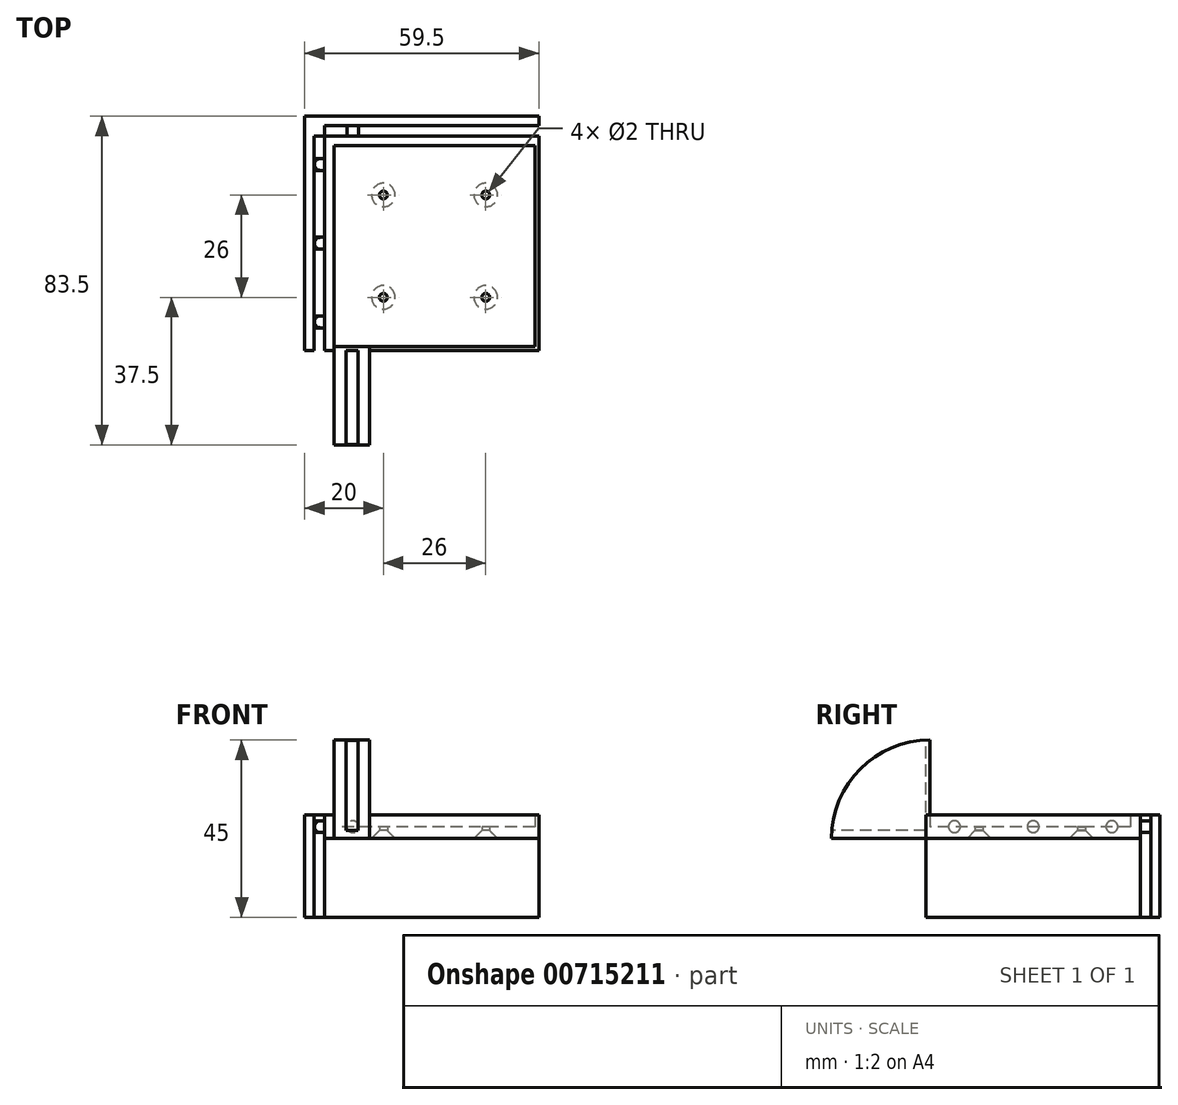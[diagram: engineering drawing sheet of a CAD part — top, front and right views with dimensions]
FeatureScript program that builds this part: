
annotation { "Feature Type Name" : "Feature", "Feature Type Description" : "" }
export const myFeature = defineFeature(function(context is Context, id is Id, definition is map)
    precondition{}
    {
        {
            var Q0;
            Q0=qCreatedBy(makeId("Top.planeOp"),FACE);
            var sketch = newSketch(context, id + "F0", { "sketchPlane" : qUnion([Q0])});
            skLineSegment(sketch, "E0.bottom", {"start": v(25.5, 25.5) * mm, "end": v(-25.5, 25.5) * mm});
            skLineSegment(sketch, "E0.top", {"start": v(25.5, -25.5) * mm, "end": v(-22.25, -25.5) * mm});
            skLineSegment(sketch, "E0.left", {"start": v(25.5, 25.5) * mm, "end": v(25.5, -25.5) * mm});
            skLineSegment(sketch, "E0.right", {"start": v(-25.5, 25.5) * mm, "end": v(-25.5, -25.5) * mm});
            skPoint(sketch, "E0.middle", {"position": v(0, 0) * mm});
            skLineSegment(sketch, "E1.0", {"start": v(28, 28) * mm, "end": v(-28, 28) * mm});
            skLineSegment(sketch, "E1.1", {"start": v(28, 28) * mm, "end": v(28, -28) * mm});
            skLineSegment(sketch, "E1.2", {"start": v(28, -28) * mm, "end": v(-22.25, -28) * mm});
            skLineSegment(sketch, "E1.3", {"start": v(-28, 28) * mm, "end": v(-28, -28) * mm});
            skCircle(sketch, "E2", {"center": v(-13, 13) * mm, "radius": 1 * mm});
            skLineSegment(sketch, "E3", {"start": v(0, 28) * mm, "end": v(0, -28) * mm, "construction": true});
            skLineSegment(sketch, "E4", {"start": v(-28, 0) * mm, "end": v(28, 0) * mm, "construction": true});
            skCircle(sketch, "E5.MirrorC", {"center": v(13, 13) * mm, "radius": 1 * mm});
            skCircle(sketch, "E6.MirrorC", {"center": v(13, -13) * mm, "radius": 1 * mm});
            skCircle(sketch, "E7.MirrorC", {"center": v(-13, -13) * mm, "radius": 1 * mm});
            skLineSegment(sketch, "E8.1", {"start": v(28, 33) * mm, "end": v(-33, 33) * mm});
            skLineSegment(sketch, "E9", {"start": v(28, 33) * mm, "end": v(28, 28) * mm});
            skLineSegment(sketch, "E10", {"start": v(-28, -28) * mm, "end": v(-33, -28) * mm});
            skLineSegment(sketch, "E11", {"start": v(28, 23.2) * mm, "end": v(28, 12.96) * mm});
            skLineSegment(sketch, "E12", {"start": v(28, 23.2) * mm, "end": v(28, 20) * mm});
            skLineSegment(sketch, "E13.trimOffspring", {"start": v(-25.25, -28) * mm, "end": v(-28, -28) * mm});
            skLineSegment(sketch, "E14", {"start": v(-25.5, -25.5) * mm, "end": v(-22.25, -25.5) * mm});
            skLineSegment(sketch, "E15", {"start": v(-25.25, -28) * mm, "end": v(-22.25, -28) * mm});
            skCircle(sketch, "E16", {"center": v(0, 0) * mm, "radius": 4.25 * mm});
            skLineSegment(sketch, "E17", {"start": v(-33, 33) * mm, "end": v(-33, -28) * mm});
            skSolve(sketch);
        }
        {
            var Q0;
            Q0=qCreatedBy(makeId("Top.planeOp"),FACE);
            var sketch = newSketch(context, id + "F1", { "sketchPlane" : qUnion([Q0])});
            skPoint(sketch, "E18.0", {"position": v(-25.5, -25.5) * mm});
            skLineSegment(sketch, "E19.bottom", {"start": v(-25.5, -25.5) * mm, "end": v(-16.5, -25.5) * mm});
            skLineSegment(sketch, "E19.top", {"start": v(-25.5, -50.5) * mm, "end": v(-16.5, -50.5) * mm});
            skLineSegment(sketch, "E19.left", {"start": v(-25.5, -25.5) * mm, "end": v(-25.5, -50.5) * mm});
            skLineSegment(sketch, "E19.right", {"start": v(-16.5, -25.5) * mm, "end": v(-16.5, -50.5) * mm});
            skLineSegment(sketch, "E20", {"start": v(-21, -50.5) * mm, "end": v(-21, -25.5) * mm, "construction": true});
            skLineSegment(sketch, "E21", {"start": v(-19.45, -25.5) * mm, "end": v(-19.45, -50.5) * mm});
            skLineSegment(sketch, "E22.MirrorCS", {"start": v(-22.55, -25.5) * mm, "end": v(-22.55, -50.5) * mm});
            skPoint(sketch, "E23.0", {"position": v(25.5, 25.5) * mm});
            skLineSegment(sketch, "E24.bottom", {"start": v(25.5, 25.5) * mm, "end": v(50.5, 25.5) * mm});
            skLineSegment(sketch, "E24.top", {"start": v(25.5, 16.5) * mm, "end": v(50.5, 16.5) * mm});
            skLineSegment(sketch, "E24.left", {"start": v(25.5, 25.5) * mm, "end": v(25.5, 16.5) * mm});
            skLineSegment(sketch, "E24.right", {"start": v(50.5, 25.5) * mm, "end": v(50.5, 16.5) * mm});
            skLineSegment(sketch, "E25", {"start": v(25.5, 21) * mm, "end": v(50.5, 21) * mm, "construction": true});
            skLineSegment(sketch, "E26", {"start": v(50.5, 22.55) * mm, "end": v(25.5, 22.55) * mm});
            skLineSegment(sketch, "E27.MirrorCS", {"start": v(50.5, 19.45) * mm, "end": v(25.5, 19.45) * mm});
            skSolve(sketch);
        }
        {
            var Q0;
            Q0=makeQuery(id+"F0.imprint","IMPRINT",FACE,{"disambiguationData":[TD([[makeQuery(id+"F0.imprint","IMPRINT",EDGE,{"derivedFrom":sQuery(id+"F0.wireOp",EDGE,"E0.bottom")}),1.0]])]});
            var Q1;
            Q1=makeQuery(id+"F0.imprint","IMPRINT",FACE,{"disambiguationData":[TD([[makeQuery(id+"F0.imprint","IMPRINT",EDGE,{"derivedFrom":sQuery(id+"F0.wireOp",EDGE,"E16")}),1.0]])]});
            extrude(context, id + "F2", {"entities" : qUnion([Q0, Q1]), "depth" : 3 * mm, "offsetDistance" : 25 * mm});
        }
        {
            var Q0;
            Q0=makeQuery(id+"F0.imprint","IMPRINT",FACE,{"disambiguationData":[TD([[makeQuery(id+"F0.imprint","IMPRINT",EDGE,{"derivedFrom":sQuery(id+"F0.wireOp",EDGE,"E0.bottom")}),-1.0]])]});
            var Q1;
            {var subQ5=sQuery(id+"F0.wireOp",EDGE,"TI18WCdd-EPFC-hNpH-Rctt-afuqL8Zf6Xfq");Q1=makeQuery(id+"F0.imprint","IMPRINT",FACE,{"disambiguationData":[TD([[makeQuery(id+"F0.imprint","IMPRINT",EDGE,{"derivedFrom":subQ5}),-1.0]])]});}
            extrude(context, id + "F3", {"entities" : qUnion([Q0, Q1]), "operationType" : NewBodyOperationType.ADD, "depth" : 6 * mm, "offsetDistance" : 25 * mm});
        }
        {
            var Q0;
            Q0=makeQuery(id+"F2.opExtrude","CAP_EDGE",EDGE,{"disambiguationData":[OSD([sQuery(id+"F0.wireOp",EDGE,"E7.MirrorC")])],"isStart":true});
            var Q1;
            Q1=makeQuery(id+"F2.opExtrude","CAP_EDGE",EDGE,{"disambiguationData":[OSD([sQuery(id+"F0.wireOp",EDGE,"E6.MirrorC")])],"isStart":true});
            var Q2;
            Q2=makeQuery(id+"F2.opExtrude","CAP_EDGE",EDGE,{"disambiguationData":[OSD([sQuery(id+"F0.wireOp",EDGE,"E5.MirrorC")])],"isStart":true});
            var Q3;
            Q3=makeQuery(id+"F2.opExtrude","CAP_EDGE",EDGE,{"disambiguationData":[OSD([sQuery(id+"F0.wireOp",EDGE,"E2")])],"isStart":true});
            chamfer(context, id + "F4", {"entities" : qUnion([Q0, Q1, Q2, Q3]), "width" : 2 * mm, "tangentPropagation" : true});
        }
        {
            var Q0;
            Q0=makeQuery(id+"FIbiUBh41szAzK7_1.boolean.opBoolean","MERGE",FACE,{"derivedFrom":[makeQuery(id+"F3.opExtrude","SWEPT_FACE",FACE,{"disambiguationData":[OSD([sQuery(id+"F0.wireOp",EDGE,"E1.2"),sQuery(id+"F0.wireOp",EDGE,"E13.trimOffspring"),sQuery(id+"F0.wireOp",EDGE,"E15")])]}),makeQuery(id+"FIbiUBh41szAzK7_1.opExtrude","SWEPT_FACE",FACE,{"disambiguationData":[OSD([sQuery(id+"F0.wireOp",EDGE,"E10")])]})]});
            extrude(context, id + "F5", {"entities" : qUnion([Q0]), "operationType" : NewBodyOperationType.REMOVE, "oppositeDirection" : true, "depth" : 1.5 * mm, "offsetDistance" : 25 * mm});
        }
        {
            var Q0;
            Q0=makeQuery(id+"FIbiUBh41szAzK7_1.boolean.opBoolean","MERGE",FACE,{"derivedFrom":[makeQuery(id+"F3.opExtrude","SWEPT_FACE",FACE,{"disambiguationData":[OSD([sQuery(id+"F0.wireOp",EDGE,"E1.1"),sQuery(id+"F0.wireOp",EDGE,"E11"),sQuery(id+"F0.wireOp",EDGE,"E12")])]}),makeQuery(id+"FIbiUBh41szAzK7_1.opExtrude","SWEPT_FACE",FACE,{"disambiguationData":[OSD([sQuery(id+"F0.wireOp",EDGE,"E9")])]})]});
            extrude(context, id + "F6", {"entities" : qUnion([Q0]), "operationType" : NewBodyOperationType.REMOVE, "oppositeDirection" : true, "depth" : 1.5 * mm, "offsetDistance" : 25 * mm});
        }
        {
            var Q0;
            {var subQ0=sQuery(id+"F1.wireOp",EDGE,"E19.right");Q0=makeQuery(id+"F1.imprint","IMPRINT",FACE,{"disambiguationData":[TD([[makeQuery(id+"F1.imprint","IMPRINT",EDGE,{"derivedFrom":subQ0}),-1.0]])]});}
            var Q1;
            {var subQ0=sQuery(id+"F1.wireOp",EDGE,"E19.left");Q1=makeQuery(id+"F1.imprint","IMPRINT",FACE,{"disambiguationData":[TD([[makeQuery(id+"F1.imprint","IMPRINT",EDGE,{"derivedFrom":subQ0}),1.0]])]});}
            extrude(context, id + "F7", {"entities" : qUnion([Q0, Q1]), "operationType" : NewBodyOperationType.ADD, "depth" : 25 * mm, "offsetDistance" : 25 * mm});
        }
        {
            var Q0;
            {var subQ0=sQuery(id+"F1.wireOp",EDGE,"E21");Q0=makeQuery(id+"F1.imprint","IMPRINT",FACE,{"disambiguationData":[TD([[makeQuery(id+"F1.imprint","IMPRINT",EDGE,{"derivedFrom":subQ0}),-1.0]])]});}
            extrude(context, id + "F8", {"entities" : qUnion([Q0]), "operationType" : NewBodyOperationType.ADD, "depth" : 2 * mm, "offsetDistance" : 25 * mm});
        }
        {
            var Q0;
            {var subQ1=sQuery(id+"F1.wireOp",EDGE,"E21");var subQ3=sQuery(id+"F0.wireOp",EDGE,"E15");var subQ4=sQuery(id+"F0.wireOp",EDGE,"E13.trimOffspring");var subQ5=sQuery(id+"F0.wireOp",EDGE,"E1.2");var subQ6=sQuery(id+"F0.wireOp",EDGE,"E14");var subQ7=sQuery(id+"F0.wireOp",EDGE,"E0.top");Q0=makeQuery(id+"F7.boolean.opBoolean","SPLIT",FACE,{"disambiguationData":[TD([makeQuery(id+"F7.opExtrude","SWEPT_FACE",FACE,{"disambiguationData":[OSD([subQ1])]})])],"derivedFrom":makeQuery(id+"F3.opExtrude","CAP_FACE",FACE,{"disambiguationData":[OSD([sQuery(id+"F0.wireOp",EDGE,"E0.bottom"),subQ7,sQuery(id+"F0.wireOp",EDGE,"E0.left"),sQuery(id+"F0.wireOp",EDGE,"E0.right"),sQuery(id+"F0.wireOp",EDGE,"E1.0"),sQuery(id+"F0.wireOp",EDGE,"E1.1"),subQ5,sQuery(id+"F0.wireOp",EDGE,"E1.3"),sQuery(id+"F0.wireOp",EDGE,"E11"),sQuery(id+"F0.wireOp",EDGE,"E12"),subQ4,subQ6,subQ3])],"isStart":false})});}
            var Q1;
            {var subQ1=sQuery(id+"F1.wireOp",EDGE,"E26");var subQ2=sQuery(id+"F0.wireOp",EDGE,"E12");var subQ3=sQuery(id+"F0.wireOp",EDGE,"E11");var subQ4=sQuery(id+"F0.wireOp",EDGE,"E1.1");var subQ6=sQuery(id+"F0.wireOp",EDGE,"E0.left");Q1=makeQuery(id+"F7.boolean.opBoolean","SPLIT",FACE,{"disambiguationData":[TD([makeQuery(id+"F7.opExtrude","SWEPT_FACE",FACE,{"disambiguationData":[OSD([subQ1])]})])],"derivedFrom":makeQuery(id+"F3.opExtrude","CAP_FACE",FACE,{"disambiguationData":[OSD([sQuery(id+"F0.wireOp",EDGE,"E0.bottom"),sQuery(id+"F0.wireOp",EDGE,"E0.top"),subQ6,sQuery(id+"F0.wireOp",EDGE,"E0.right"),sQuery(id+"F0.wireOp",EDGE,"E1.0"),subQ4,sQuery(id+"F0.wireOp",EDGE,"E1.2"),sQuery(id+"F0.wireOp",EDGE,"E1.3"),subQ3,subQ2,sQuery(id+"F0.wireOp",EDGE,"E13.trimOffspring"),sQuery(id+"F0.wireOp",EDGE,"E14"),sQuery(id+"F0.wireOp",EDGE,"E15")])],"isStart":false})});}
            var Q2;
            Q2=makeQuery(id+"F7.opExtrude","CAP_FACE",FACE,{"disambiguationData":[OSD([sQuery(id+"F1.wireOp",EDGE,"E19.bottom"),sQuery(id+"F1.wireOp",EDGE,"E19.top"),sQuery(id+"F1.wireOp",EDGE,"E19.left"),sQuery(id+"F1.wireOp",EDGE,"E22.MirrorCS")])],"isStart":false});
            var Q3;
            Q3=makeQuery(id+"F2.opExtrude","SWEPT_BODY",BODY,{"disambiguationData":[OSD([sQuery(id+"F0.wireOp",EDGE,"E0.bottom"),sQuery(id+"F0.wireOp",EDGE,"E0.top"),sQuery(id+"F0.wireOp",EDGE,"E0.left"),sQuery(id+"F0.wireOp",EDGE,"E0.right"),sQuery(id+"F0.wireOp",EDGE,"E2"),sQuery(id+"F0.wireOp",EDGE,"E5.MirrorC"),sQuery(id+"F0.wireOp",EDGE,"E6.MirrorC"),sQuery(id+"F0.wireOp",EDGE,"E7.MirrorC"),sQuery(id+"F0.wireOp",EDGE,"E14"),sQuery(id+"F0.wireOp",EDGE,"E16")])]});
            extrude(context, id + "F9", {"entities" : qUnion([Q0, Q1]), "operationType" : NewBodyOperationType.ADD, "endBound" : BoundingType.UP_TO_SURFACE, "depth" : 25 * mm, "endBoundEntityFace" : qUnion([Q2]), "endBoundEntityBody" : qUnion([Q3]), "offsetDistance" : 25 * mm});
        }
        {
            var Q0;
            {var subQ0=sQuery(id+"F1.wireOp",EDGE,"E19.top");Q0=makeQuery(id+"F7.opExtrude","CAP_EDGE",EDGE,{"disambiguationData":[OSD([subQ0]),TDD([makeQuery(id+"F1.imprint","IMPRINT",EDGE,{"disambiguationData":[TD([[makeQuery(id+"F1.imprint","INTERSECT",VERTEX,{"derivedFrom":[subQ0,sQuery(id+"F1.wireOp",EDGE,"E19.left")]}),-1.0]])],"derivedFrom":subQ0})])],"isStart":false});}
            var Q1;
            {var subQ0=sQuery(id+"F1.wireOp",EDGE,"E19.top");Q1=makeQuery(id+"F7.opExtrude","CAP_EDGE",EDGE,{"disambiguationData":[OSD([subQ0]),TDD([makeQuery(id+"F1.imprint","IMPRINT",EDGE,{"disambiguationData":[TD([[makeQuery(id+"F1.imprint","INTERSECT",VERTEX,{"derivedFrom":[subQ0,sQuery(id+"F1.wireOp",EDGE,"E19.right")]}),1.0]])],"derivedFrom":subQ0})])],"isStart":false});}
            var Q2;
            {var subQ0=sQuery(id+"F1.wireOp",EDGE,"E24.right");Q2=makeQuery(id+"F7.opExtrude","CAP_EDGE",EDGE,{"disambiguationData":[OSD([subQ0]),TDD([makeQuery(id+"F1.imprint","IMPRINT",EDGE,{"disambiguationData":[TD([[makeQuery(id+"F1.imprint","INTERSECT",VERTEX,{"derivedFrom":[sQuery(id+"F1.wireOp",EDGE,"E24.bottom"),subQ0]}),-1.0]])],"derivedFrom":subQ0})])],"isStart":false});}
            fillet(context, id + "F10", {"entities" : qUnion([Q0, Q1, Q2]), "radius" : 25 * mm, "tangentPropagation" : true, "allowEdgeOverflow" : false});
        }
        {
            var Q0;
            Q0=makeQuery(id+"F3.opExtrude","SWEPT_FACE",FACE,{"disambiguationData":[OSD([sQuery(id+"F0.wireOp",EDGE,"E1.3")])]});
            var sketch = newSketch(context, id + "F11", { "sketchPlane" : qUnion([Q0])});
            skCircle(sketch, "E28", {"center": v(-20.75, 3) * mm, "radius": 1.5 * mm});
            skPoint(sketch, "E28.centerSnap0", {"position": v(-28, 3) * mm});
            skCircle(sketch, "E29", {"center": v(19.25, 3) * mm, "radius": 1.5 * mm});
            skCircle(sketch, "E30", {"center": v(-0.75, 3) * mm, "radius": 1.5 * mm});
            skPoint(sketch, "E30.centerSnap0", {"position": v(-0.75, 6) * mm});
            skSolve(sketch);
        }
        {
            var Q0;
            Q0=makeQuery(id+"F11.imprint","IMPRINT",FACE,{"disambiguationData":[TD([[makeQuery(id+"F11.imprint","IMPRINT",EDGE,{"derivedFrom":sQuery(id+"F11.wireOp",EDGE,"E28")}),1.0]])]});
            var Q1;
            Q1=makeQuery(id+"F11.imprint","IMPRINT",FACE,{"disambiguationData":[TD([[makeQuery(id+"F11.imprint","IMPRINT",EDGE,{"derivedFrom":sQuery(id+"F11.wireOp",EDGE,"E30")}),1.0]])]});
            var Q2;
            Q2=makeQuery(id+"F11.imprint","IMPRINT",FACE,{"disambiguationData":[TD([[makeQuery(id+"F11.imprint","IMPRINT",EDGE,{"derivedFrom":sQuery(id+"F11.wireOp",EDGE,"E29")}),1.0]])]});
            extrude(context, id + "F12", {"entities" : qUnion([Q0, Q1, Q2]), "operationType" : NewBodyOperationType.ADD, "depth" : 2.5 * mm, "offsetDistance" : 25 * mm});
        }
        {
            var Q0;
            Q0=makeQuery(id+"F3.opExtrude","SWEPT_FACE",FACE,{"disambiguationData":[OSD([sQuery(id+"F0.wireOp",EDGE,"E1.0")])]});
            var sketch = newSketch(context, id + "F13", { "sketchPlane" : qUnion([Q0])});
            skCircle(sketch, "E31", {"center": v(0.75, 3) * mm, "radius": 1.5 * mm});
            skPoint(sketch, "E31.centerSnap0", {"position": v(28, 3) * mm});
            skPoint(sketch, "E31.centerSnap1", {"position": v(0.75, 6) * mm});
            skCircle(sketch, "E32", {"center": v(20.75, 3) * mm, "radius": 1.5 * mm});
            skCircle(sketch, "E33", {"center": v(-19.25, 3) * mm, "radius": 1.5 * mm});
            skSolve(sketch);
        }
        {
            var Q0;
            Q0=makeQuery(id+"F13.imprint","IMPRINT",FACE,{"disambiguationData":[TD([[makeQuery(id+"F13.imprint","IMPRINT",EDGE,{"derivedFrom":sQuery(id+"F13.wireOp",EDGE,"E33")}),1.0]])]});
            var Q1;
            Q1=makeQuery(id+"F13.imprint","IMPRINT",FACE,{"disambiguationData":[TD([[makeQuery(id+"F13.imprint","IMPRINT",EDGE,{"derivedFrom":sQuery(id+"F13.wireOp",EDGE,"E31")}),1.0]])]});
            extrude(context, id + "F14", {"entities" : qUnion([Q0, Q1]), "operationType" : NewBodyOperationType.ADD, "depth" : 2.5 * mm, "offsetDistance" : 25 * mm});
        }
        {
            var Q0;
            Q0=makeQuery(id+"F12.opExtrude","CAP_FACE",FACE,{"disambiguationData":[OSD([sQuery(id+"F11.wireOp",EDGE,"E28")])],"isStart":false});
            var Q1;
            Q1=makeQuery(id+"F12.opExtrude","CAP_FACE",FACE,{"disambiguationData":[OSD([sQuery(id+"F11.wireOp",EDGE,"E30")])],"isStart":false});
            var Q2;
            Q2=makeQuery(id+"F12.opExtrude","CAP_FACE",FACE,{"disambiguationData":[OSD([sQuery(id+"F11.wireOp",EDGE,"E29")])],"isStart":false});
            var Q3;
            Q3=makeQuery(id+"F14.opExtrude","CAP_FACE",FACE,{"disambiguationData":[OSD([sQuery(id+"F13.wireOp",EDGE,"E33")])],"isStart":false});
            var Q4;
            Q4=makeQuery(id+"F14.opExtrude","CAP_FACE",FACE,{"disambiguationData":[OSD([sQuery(id+"F13.wireOp",EDGE,"E31")])],"isStart":false});
            fillet(context, id + "F15", {"entities" : qUnion([Q0, Q1, Q2, Q3, Q4]), "radius" : 1.5 * mm, "tangentPropagation" : true, "allowEdgeOverflow" : false});
        }
        {
            var Q0;
            Q0=makeQuery(id+"F0.imprint","IMPRINT",FACE,{"disambiguationData":[TD([[makeQuery(id+"F0.imprint","IMPRINT",EDGE,{"derivedFrom":sQuery(id+"F0.wireOp",EDGE,"E1.0")}),-1.0]])]});
            extrude(context, id + "F16", {"entities" : qUnion([Q0]), "depth" : 6 * mm, "offsetDistance" : 25 * mm, "hasSecondDirection" : true, "secondDirectionOppositeDirection" : true, "secondDirectionDepth" : 20 * mm});
        }
        {
            var Q0;
            Q0=makeQuery(id+"F16.opExtrude","SWEPT_FACE",FACE,{"disambiguationData":[OSD([sQuery(id+"F0.wireOp",EDGE,"E9")])]});
            extrude(context, id + "F17", {"entities" : qUnion([Q0]), "operationType" : NewBodyOperationType.REMOVE, "oppositeDirection" : true, "depth" : 1.5 * mm, "offsetDistance" : 25 * mm});
        }
        {
            var Q0;
            Q0=makeQuery(id+"F16.opExtrude","SWEPT_FACE",FACE,{"disambiguationData":[OSD([sQuery(id+"F0.wireOp",EDGE,"E10")])]});
            extrude(context, id + "F18", {"entities" : qUnion([Q0]), "operationType" : NewBodyOperationType.REMOVE, "oppositeDirection" : true, "depth" : 1.5 * mm, "offsetDistance" : 25 * mm});
        }
        {
            var Q0;
            Q0=makeQuery(id+"F16.opExtrude","SWEPT_FACE",FACE,{"disambiguationData":[OSD([sQuery(id+"F0.wireOp",EDGE,"E1.3")])]});
            var sketch = newSketch(context, id + "F19", { "sketchPlane" : qUnion([Q0])});
            skCircle(sketch, "E34.0", {"center": v(20.75, 3) * mm, "radius": 1.5 * mm});
            skCircle(sketch, "E34.1", {"center": v(0.75, 3) * mm, "radius": 1.5 * mm});
            skCircle(sketch, "E34.2", {"center": v(-19.25, 3) * mm, "radius": 1.5 * mm});
            skSolve(sketch);
        }
        {
            var Q0;
            Q0=makeQuery(id+"F16.opExtrude","SWEPT_FACE",FACE,{"disambiguationData":[OSD([sQuery(id+"F0.wireOp",EDGE,"E1.0")])]});
            var sketch = newSketch(context, id + "F20", { "sketchPlane" : qUnion([Q0])});
            skCircle(sketch, "E35.0", {"center": v(-20.75, 3) * mm, "radius": 1.5 * mm});
            skCircle(sketch, "E35.1", {"center": v(-0.75, 3) * mm, "radius": 1.5 * mm});
            skCircle(sketch, "E35.2", {"center": v(19.25, 3) * mm, "radius": 1.5 * mm});
            skSolve(sketch);
        }
        {
            var Q0;
            Q0=makeQuery(id+"F20.imprint","IMPRINT",FACE,{"disambiguationData":[TD([[makeQuery(id+"F20.imprint","IMPRINT",EDGE,{"derivedFrom":sQuery(id+"F20.wireOp",EDGE,"E35.0")}),-1.0]])]});
            var Q1;
            Q1=makeQuery(id+"F13.imprint","IMPRINT",FACE,{"disambiguationData":[TD([[makeQuery(id+"F13.imprint","IMPRINT",EDGE,{"derivedFrom":sQuery(id+"F13.wireOp",EDGE,"E31")}),1.0]])]});
            var Q2;
            Q2=makeQuery(id+"F13.imprint","IMPRINT",FACE,{"disambiguationData":[TD([[makeQuery(id+"F13.imprint","IMPRINT",EDGE,{"derivedFrom":sQuery(id+"F13.wireOp",EDGE,"E33")}),1.0]])]});
            extrude(context, id + "F21", {"entities" : qUnion([Q0, Q1, Q2]), "operationType" : NewBodyOperationType.REMOVE, "oppositeDirection" : true, "depth" : 2.6 * mm, "offsetDistance" : 25 * mm});
        }
        {
            var Q0;
            Q0=makeQuery(id+"F19.imprint","IMPRINT",FACE,{"disambiguationData":[TD([[makeQuery(id+"F19.imprint","IMPRINT",EDGE,{"derivedFrom":sQuery(id+"F19.wireOp",EDGE,"E34.0")}),-1.0]])]});
            var Q1;
            Q1=makeQuery(id+"F19.imprint","IMPRINT",FACE,{"disambiguationData":[TD([[makeQuery(id+"F19.imprint","IMPRINT",EDGE,{"derivedFrom":sQuery(id+"F19.wireOp",EDGE,"E34.1")}),-1.0]])]});
            var Q2;
            Q2=makeQuery(id+"F19.imprint","IMPRINT",FACE,{"disambiguationData":[TD([[makeQuery(id+"F19.imprint","IMPRINT",EDGE,{"derivedFrom":sQuery(id+"F19.wireOp",EDGE,"E34.2")}),-1.0]])]});
            extrude(context, id + "F22", {"entities" : qUnion([Q0, Q1, Q2]), "operationType" : NewBodyOperationType.REMOVE, "oppositeDirection" : true, "depth" : 2.6 * mm, "offsetDistance" : 25 * mm});
        }
    });
